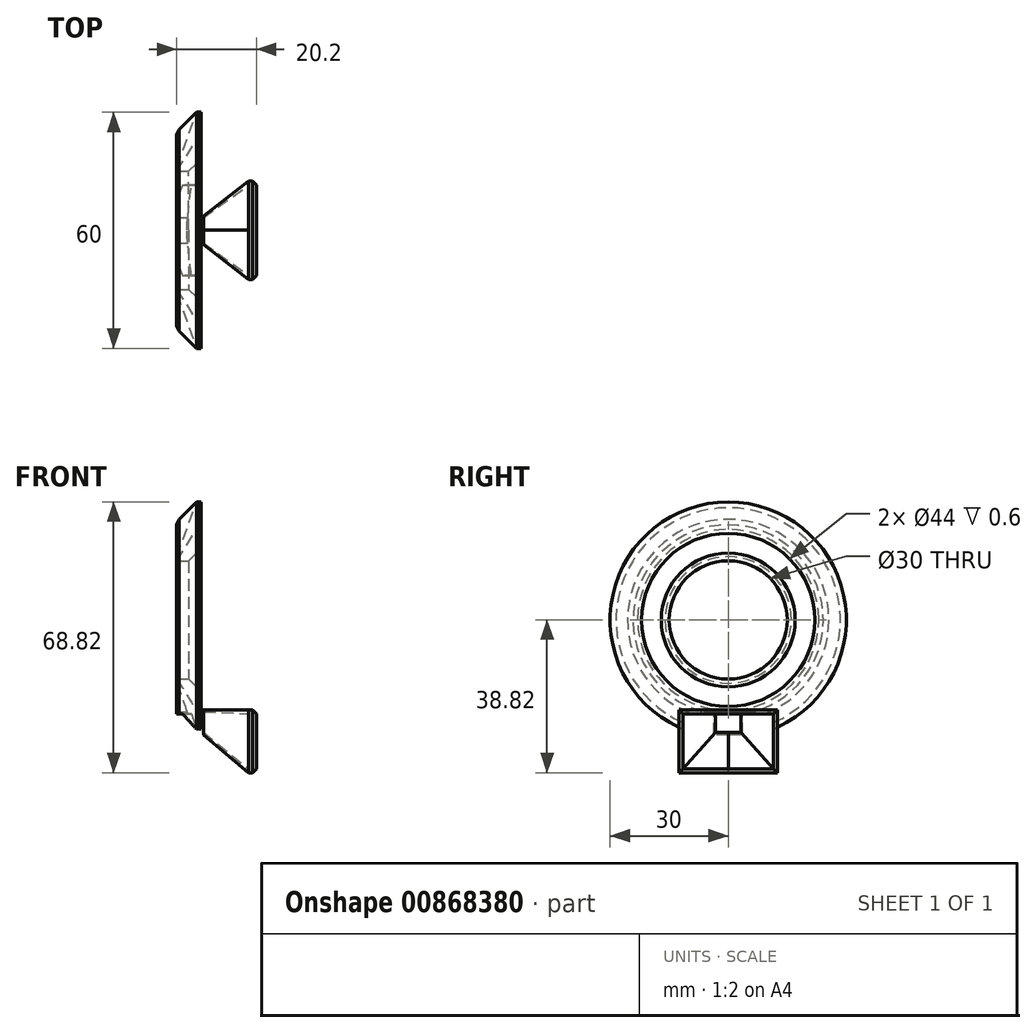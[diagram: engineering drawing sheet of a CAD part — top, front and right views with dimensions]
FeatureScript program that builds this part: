
annotation { "Feature Type Name" : "Feature", "Feature Type Description" : "" }
export const myFeature = defineFeature(function(context is Context, id is Id, definition is map)
    precondition{}
    {
        {
            var Q0;
            Q0=qCreatedBy(makeId("Front.planeOp"),FACE);
            var sketch = newSketch(context, id + "F0", { "sketchPlane" : qUnion([Q0])});
            skLineSegment(sketch, "E0.bottom", {"start": v(-2.5, 15) * mm, "end": v(2.5, 15) * mm});
            skLineSegment(sketch, "E0.top", {"start": v(-2.5, -15) * mm, "end": v(2.5, -15) * mm});
            skLineSegment(sketch, "E0.left", {"start": v(-2.5, 15) * mm, "end": v(-2.5, -15) * mm});
            skLineSegment(sketch, "E0.right", {"start": v(2.5, 15) * mm, "end": v(2.5, -15) * mm});
            skPoint(sketch, "E0.middle", {"position": v(0, 0) * mm});
            skLineSegment(sketch, "E1", {"start": v(2.5, 23) * mm, "end": v(2.5, 15) * mm});
            skLineSegment(sketch, "E2", {"start": v(-8.2, -15) * mm, "end": v(-8.2, 23) * mm});
            skLineSegment(sketch, "E3", {"start": v(2.5, 23) * mm, "end": v(-2.5, 15) * mm});
            skLineSegment(sketch, "E4", {"start": v(-2.5, 15) * mm, "end": v(-2.5, 30) * mm});
            skLineSegment(sketch, "E5", {"start": v(-2.5, 16.07) * mm, "end": v(2.5, 30) * mm});
            skLineSegment(sketch, "E6", {"start": v(-2.5, 30) * mm, "end": v(2.5, 30) * mm});
            skLineSegment(sketch, "E7", {"start": v(2.5, 0) * mm, "end": v(-2.5, 0) * mm});
            skLineSegment(sketch, "E8.bottom", {"start": v(2.5, 15) * mm, "end": v(-2.5, 15) * mm});
            skLineSegment(sketch, "E8.top", {"start": v(2.5, 12.99) * mm, "end": v(-2.5, 12.99) * mm});
            skLineSegment(sketch, "E8.left", {"start": v(2.5, 15) * mm, "end": v(2.5, 12.99) * mm});
            skLineSegment(sketch, "E8.right", {"start": v(-2.5, 15) * mm, "end": v(-2.5, 12.99) * mm});
            skSolve(sketch);
        }
        {
            var Q0;
            {var subQ2=sQuery(id+"F0.wireOp",EDGE,"E5");Q0=makeQuery(id+"F0.imprint","IMPRINT",FACE,{"disambiguationData":[TD([[makeQuery(id+"F0.imprint","IMPRINT",EDGE,{"derivedFrom":subQ2}),1.0]])]});}
            var Q1;
            Q1=makeQuery(id+"F0.imprint","IMPRINT",FACE,{"disambiguationData":[TD([[makeQuery(id+"F0.imprint","IMPRINT",EDGE,{"derivedFrom":sQuery(id+"F0.wireOp",EDGE,"E0.bottom")}),1.0]])]});
            var Q2;
            Q2=makeQuery(id+"F0.imprint","IMPRINT",FACE,{"disambiguationData":[TD([[makeQuery(id+"F0.imprint","IMPRINT",EDGE,{"derivedFrom":sQuery(id+"F0.wireOp",EDGE,"E8.bottom")}),1.0]])]});
            var Q3;
            Q3=makeQuery(id+"F0.imprint","IMPRINT",FACE,{"disambiguationData":[TD([[makeQuery(id+"F0.imprint","IMPRINT",EDGE,{"derivedFrom":sQuery(id+"F0.wireOp",EDGE,"E1")}),-1.0]])]});
            var Q4;
            Q4=sQuery(id+"F0.wireOp",EDGE,"E7");
            revolve(context, id + "F1", {"surfaceOperationType" : NewSurfaceOperationType.NEW, "entities" : qUnion([Q0, Q1, Q2, Q3]), "axis" : qUnion([Q4]), "revolveType" : RevolveType.FULL});
        }
        {
            var Q0;
            Q0=makeQuery(id+"F1.opRevolve","SWEPT_EDGE",EDGE,{"disambiguationData":[OSD([sQuery(id+"F0.wireOp",EDGE,"E4"),sQuery(id+"F0.wireOp",EDGE,"E6")])]});
            chamfer(context, id + "F2", {"entities" : qUnion([Q0]), "width" : 5 * mm, "tangentPropagation" : true});
        }
        {
            var Q0;
            Q0=makeQuery(id+"F1.opRevolve","SWEPT_EDGE",EDGE,{"disambiguationData":[OSD([sQuery(id+"F0.wireOp",EDGE,"E0.right"),sQuery(id+"F0.wireOp",EDGE,"E8.top"),sQuery(id+"F0.wireOp",EDGE,"E8.left")])]});
            chamfer(context, id + "F3", {"entities" : qUnion([Q0]), "width" : 2 * mm, "tangentPropagation" : true});
        }
        {
            var Q0;
            {var subQ0=sQuery(id+"F0.wireOp",EDGE,"E4");Q0=makeQuery(id+"F2.opChamfer","BLEND_EDGE",EDGE,{"blendedFrom":[makeQuery(id+"F1.opRevolve","SWEPT_EDGE",EDGE,{"disambiguationData":[OSD([subQ0,sQuery(id+"F0.wireOp",EDGE,"E6")])]}),makeQuery(id+"F1.opRevolve","SWEPT_FACE",FACE,{"disambiguationData":[OSD([subQ0])]})],"blendedInto":[makeQuery(id+"F1.opRevolve","SWEPT_FACE",FACE,{"disambiguationData":[OSD([subQ0])]})]});}
            chamfer(context, id + "F4", {"entities" : qUnion([Q0]), "width" : 2 * mm, "tangentPropagation" : true});
        }
        {
            var Q0;
            Q0=makeQuery(id+"F1.opRevolve","SWEPT_FACE",FACE,{"disambiguationData":[OSD([sQuery(id+"F0.wireOp",EDGE,"E1"),sQuery(id+"F0.wireOp",EDGE,"E8.left")])]});
            var sketch = newSketch(context, id + "F5", { "sketchPlane" : qUnion([Q0])});
            skCircle(sketch, "E9", {"center": v(0, 0) * mm, "radius": 23 * mm});
            skCircle(sketch, "E10", {"center": v(0, 0) * mm, "radius": 22 * mm});
            skCircle(sketch, "E11", {"center": v(0, 0) * mm, "radius": 30 * mm});
            skCircle(sketch, "E12", {"center": v(0, 0) * mm, "radius": 28.5 * mm});
            skSolve(sketch);
        }
        {
            var Q0;
            Q0=makeQuery(id+"F5.imprint","IMPRINT",FACE,{"disambiguationData":[TD([[makeQuery(id+"F5.imprint","IMPRINT",EDGE,{"derivedFrom":sQuery(id+"F5.wireOp",EDGE,"E9")}),1.0]])]});
            var Q1;
            Q1=makeQuery(id+"F5.imprint","IMPRINT",FACE,{"disambiguationData":[TD([[makeQuery(id+"F5.imprint","IMPRINT",EDGE,{"derivedFrom":sQuery(id+"F5.wireOp",EDGE,"E11")}),1.0]])]});
            extrude(context, id + "F6", {"entities" : qUnion([Q0, Q1]), "operationType" : NewBodyOperationType.ADD, "depth" : .6 * mm, "offsetDistance" : 25 * mm});
        }
        {
            var Q0;
            Q0=makeQuery(id+"F6.opExtrude","CAP_FACE",FACE,{"disambiguationData":[OSD([sQuery(id+"F5.wireOp",EDGE,"E9"),sQuery(id+"F5.wireOp",EDGE,"E10")])],"isStart":false});
            var sketch = newSketch(context, id + "F7", { "sketchPlane" : qUnion([Q0])});
            skCircle(sketch, "E13", {"center": v(0, 0) * mm, "radius": 30 * mm});
            skCircle(sketch, "E14", {"center": v(0, 0) * mm, "radius": 22 * mm});
            skSolve(sketch);
        }
        {
            var Q0;
            Q0 = qSketchRegion(id + "F7", true);
            extrude(context, id + "F8", {"entities" : qUnion([Q0]), "depth" : .6 * mm, "offsetDistance" : 25 * mm});
        }
        {
            var Q0;
            Q0=makeQuery(id+"F8.opExtrude","CAP_FACE",FACE,{"disambiguationData":[OSD([sQuery(id+"F7.wireOp",EDGE,"E13"),sQuery(id+"F7.wireOp",EDGE,"E14")])],"isStart":false});
            var sketch = newSketch(context, id + "F9", { "sketchPlane" : qUnion([Q0])});
            skLineSegment(sketch, "E15", {"start": v(0, -30) * mm, "end": v(0, -22) * mm});
            skLineSegment(sketch, "E16.bottom", {"start": v(3.6, -29.18) * mm, "end": v(-3.6, -29.18) * mm});
            skLineSegment(sketch, "E16.top", {"start": v(3.6, -22.82) * mm, "end": v(-3.6, -22.82) * mm});
            skLineSegment(sketch, "E16.left", {"start": v(3.6, -29.18) * mm, "end": v(3.6, -22.82) * mm});
            skLineSegment(sketch, "E16.right", {"start": v(-3.6, -29.18) * mm, "end": v(-3.6, -22.82) * mm});
            skPoint(sketch, "E16.middle", {"position": v(0, -26) * mm});
            skSolve(sketch);
        }
        {
            var Q0;
            Q0 = qSketchRegion(id + "F9", true);
            extrude(context, id + "F10", {"entities" : qUnion([Q0]), "operationType" : NewBodyOperationType.ADD, "depth" : .6 * mm, "offsetDistance" : 25 * mm});
        }
        {
            var Q0;
            Q0=makeQuery(id+"F10.opExtrude","SWEPT_FACE",FACE,{"disambiguationData":[OSD([sQuery(id+"F9.wireOp",EDGE,"E16.top")])]});
            var sketch = newSketch(context, id + "F11", { "sketchPlane" : qUnion([Q0])});
            skLineSegment(sketch, "E17.bottom", {"start": v(17.44, -6.08) * mm, "end": v(-9.45, -6.08) * mm});
            skLineSegment(sketch, "E17.top", {"start": v(17.44, 12.53) * mm, "end": v(-9.45, 12.53) * mm});
            skLineSegment(sketch, "E17.left", {"start": v(17.44, -6.08) * mm, "end": v(17.44, 12.53) * mm});
            skLineSegment(sketch, "E17.right", {"start": v(-9.45, -6.08) * mm, "end": v(-9.45, 12.53) * mm});
            skPoint(sketch, "E17.middle", {"position": v(4, 3.23) * mm});
            skLineSegment(sketch, "E18", {"start": v(3.7, 0) * mm, "end": v(16.7, 0) * mm});
            skLineSegment(sketch, "E19.bottom", {"start": v(15.7, 12.5) * mm, "end": v(17.7, 12.5) * mm});
            skLineSegment(sketch, "E19.top", {"start": v(15.7, -12.5) * mm, "end": v(17.7, -12.5) * mm});
            skLineSegment(sketch, "E19.left", {"start": v(15.7, 12.5) * mm, "end": v(15.7, -12.5) * mm});
            skLineSegment(sketch, "E19.right", {"start": v(17.7, 12.5) * mm, "end": v(17.7, -12.5) * mm});
            skPoint(sketch, "E19.middle", {"position": v(16.7, 0) * mm});
            skSolve(sketch);
        }
        {
            var Q0;
            {var subQ3=sQuery(id+"F11.wireOp",EDGE,"E19.bottom");Q0=makeQuery(id+"F11.imprint","IMPRINT",FACE,{"disambiguationData":[TD([[makeQuery(id+"F11.imprint","IMPRINT",EDGE,{"derivedFrom":subQ3}),-1.0]])]});}
            var Q1;
            {var subQ5=sQuery(id+"F11.wireOp",EDGE,"E19.top");Q1=makeQuery(id+"F11.imprint","IMPRINT",FACE,{"disambiguationData":[TD([[makeQuery(id+"F11.imprint","IMPRINT",EDGE,{"derivedFrom":subQ5}),1.0]])]});}
            extrude(context, id + "F12", {"entities" : qUnion([Q0, Q1]), "operationType" : NewBodyOperationType.ADD, "depth" : -16 * mm, "offsetDistance" : 25 * mm});
        }
        {
            var Q0;
            Q0=makeQuery(id+"F10.opExtrude","CAP_FACE",FACE,{"disambiguationData":[OSD([sQuery(id+"F9.wireOp",EDGE,"E16.bottom"),sQuery(id+"F9.wireOp",EDGE,"E16.top"),sQuery(id+"F9.wireOp",EDGE,"E16.left"),sQuery(id+"F9.wireOp",EDGE,"E16.right")])],"isStart":false});
            var sketch = newSketch(context, id + "F13", { "sketchPlane" : qUnion([Q0])});
            skLineSegment(sketch, "E20", {"start": v(0, -22.82) * mm, "end": v(0, -29.18) * mm});
            skLineSegment(sketch, "E21.bottom", {"start": v(-3.23, -28.62) * mm, "end": v(3.23, -28.62) * mm});
            skLineSegment(sketch, "E21.top", {"start": v(-3.23, -23.38) * mm, "end": v(3.23, -23.38) * mm});
            skLineSegment(sketch, "E21.left", {"start": v(-3.23, -28.62) * mm, "end": v(-3.23, -23.38) * mm});
            skLineSegment(sketch, "E21.right", {"start": v(3.23, -28.62) * mm, "end": v(3.23, -23.38) * mm});
            skPoint(sketch, "E21.middle", {"position": v(0, -26) * mm});
            skSolve(sketch);
        }
        {
            var Q0;
            Q0=makeQuery(id+"F12.opExtrude","SWEPT_FACE",FACE,{"disambiguationData":[OSD([sQuery(id+"F11.wireOp",EDGE,"E19.left")])]});
            var sketch = newSketch(context, id + "F14", { "sketchPlane" : qUnion([Q0])});
            skLineSegment(sketch, "E22", {"start": v(0, -38.82) * mm, "end": v(0, -22.82) * mm});
            skLineSegment(sketch, "E23.bottom", {"start": v(11.5, -37.82) * mm, "end": v(-11.5, -37.82) * mm});
            skLineSegment(sketch, "E23.top", {"start": v(11.5, -23.82) * mm, "end": v(-11.5, -23.82) * mm});
            skLineSegment(sketch, "E23.left", {"start": v(11.5, -37.82) * mm, "end": v(11.5, -23.82) * mm});
            skLineSegment(sketch, "E23.right", {"start": v(-11.5, -37.82) * mm, "end": v(-11.5, -23.82) * mm});
            skPoint(sketch, "E23.middle", {"position": v(0, -30.82) * mm});
            skSolve(sketch);
        }
        {
            var Q0;
            Q0=makeQuery(id+"F12.opExtrude","SWEPT_FACE",FACE,{"disambiguationData":[OSD([sQuery(id+"F11.wireOp",EDGE,"E19.right")])]});
            var sketch = newSketch(context, id + "F15", { "sketchPlane" : qUnion([Q0])});
            skLineSegment(sketch, "E24", {"start": v(0, -22.82) * mm, "end": v(0, -38.82) * mm});
            skLineSegment(sketch, "E25.bottom", {"start": v(-11.5, -23.82) * mm, "end": v(11.5, -23.82) * mm});
            skLineSegment(sketch, "E25.top", {"start": v(-11.5, -37.82) * mm, "end": v(11.5, -37.82) * mm});
            skLineSegment(sketch, "E25.left", {"start": v(-11.5, -23.82) * mm, "end": v(-11.5, -37.82) * mm});
            skLineSegment(sketch, "E25.right", {"start": v(11.5, -23.82) * mm, "end": v(11.5, -37.82) * mm});
            skPoint(sketch, "E25.middle", {"position": v(0, -30.82) * mm});
            skSolve(sketch);
        }
        {
            var Q0;
            {var subQ5=sQuery(id+"F15.wireOp",EDGE,"E25.right");Q0=makeQuery(id+"F15.imprint","IMPRINT",FACE,{"disambiguationData":[TD([[makeQuery(id+"F15.imprint","IMPRINT",EDGE,{"derivedFrom":subQ5}),-1.0]])]});}
            var Q1;
            {var subQ5=sQuery(id+"F15.wireOp",EDGE,"E25.left");Q1=makeQuery(id+"F15.imprint","IMPRINT",FACE,{"disambiguationData":[TD([[makeQuery(id+"F15.imprint","IMPRINT",EDGE,{"derivedFrom":subQ5}),1.0]])]});}
            extrude(context, id + "F16", {"entities" : qUnion([Q0, Q1]), "operationType" : NewBodyOperationType.REMOVE, "oppositeDirection" : true, "depth" : 25 * mm, "offsetDistance" : 25 * mm});
        }
        {
            var Q2;
            {var subQ5=sQuery(id+"F14.wireOp",EDGE,"E23.left");Q2=makeQuery(id+"F14.imprint","IMPRINT",FACE,{"disambiguationData":[TD([[makeQuery(id+"F14.imprint","IMPRINT",EDGE,{"derivedFrom":subQ5}),1.0]])]});}
            var Q3;
            {var subQ5=sQuery(id+"F13.wireOp",EDGE,"E21.left");Q3=makeQuery(id+"F13.imprint","IMPRINT",FACE,{"disambiguationData":[TD([[makeQuery(id+"F13.imprint","IMPRINT",EDGE,{"derivedFrom":subQ5}),-1.0]])]});}
            loft(context, id + "F17", {"operationType" : NewBodyOperationType.REMOVE, "sheetProfilesArray" : [{ "sheetProfileEntities" : qUnion([Q2]) }, { "sheetProfileEntities" : qUnion([Q3]) }]});
        }
        {
            var Q0;
            {var subQ5=sQuery(id+"F13.wireOp",EDGE,"E21.left");Q0=makeQuery(id+"F13.imprint","IMPRINT",FACE,{"disambiguationData":[TD([[makeQuery(id+"F13.imprint","IMPRINT",EDGE,{"derivedFrom":subQ5}),-1.0]])]});}
            var Q1;
            {var subQ5=sQuery(id+"F13.wireOp",EDGE,"E21.right");Q1=makeQuery(id+"F13.imprint","IMPRINT",FACE,{"disambiguationData":[TD([[makeQuery(id+"F13.imprint","IMPRINT",EDGE,{"derivedFrom":subQ5}),1.0]])]});}
            extrude(context, id + "F18", {"entities" : qUnion([Q0, Q1]), "operationType" : NewBodyOperationType.REMOVE, "oppositeDirection" : true, "depth" : 25 * mm, "offsetDistance" : 25 * mm});
        }
        {
            var Q0;
            {var subQ0=sQuery(id+"F13.wireOp",EDGE,"E21.left");Q0=makeQuery(id+"F13.imprint","IMPRINT",FACE,{"disambiguationData":[TD([[makeQuery(id+"F13.imprint","IMPRINT",EDGE,{"derivedFrom":subQ0}),1.0]])]});}
            var Q1;
            {var subQ0=sQuery(id+"F14.wireOp",EDGE,"E23.left");Q1=makeQuery(id+"F14.imprint","IMPRINT",FACE,{"disambiguationData":[TD([[makeQuery(id+"F14.imprint","IMPRINT",EDGE,{"derivedFrom":subQ0}),-1.0]])]});}
            loft(context, id + "F19", {"sheetProfilesArray" : [{ "sheetProfileEntities" : qUnion([Q0]) }, { "sheetProfileEntities" : qUnion([Q1]) }]});
        }
        {
            var Q0;
            {var subQ0=sQuery(id+"F13.wireOp",EDGE,"E21.right");Q0=makeQuery(id+"F13.imprint","IMPRINT",FACE,{"disambiguationData":[TD([[makeQuery(id+"F13.imprint","IMPRINT",EDGE,{"derivedFrom":subQ0}),-1.0]])]});}
            var Q1;
            {var subQ0=sQuery(id+"F14.wireOp",EDGE,"E23.right");Q1=makeQuery(id+"F14.imprint","IMPRINT",FACE,{"disambiguationData":[TD([[makeQuery(id+"F14.imprint","IMPRINT",EDGE,{"derivedFrom":subQ0}),1.0]])]});}
            loft(context, id + "F20", {"sheetProfilesArray" : [{ "sheetProfileEntities" : qUnion([Q0]) }, { "sheetProfileEntities" : qUnion([Q1]) }]});
        }
        {
            var Q0;
            Q0=makeQuery(id+"F12.opExtrude","CAP_EDGE",EDGE,{"disambiguationData":[OSD([sQuery(id+"F11.wireOp",EDGE,"E19.right")])],"isStart":true});
            var Q1;
            Q1=makeQuery(id+"F12.opExtrude","CAP_EDGE",EDGE,{"disambiguationData":[OSD([sQuery(id+"F11.wireOp",EDGE,"E19.right")])],"isStart":false});
            var Q2;
            Q2=makeQuery(id+"F12.opExtrude","SWEPT_EDGE",EDGE,{"disambiguationData":[OSD([sQuery(id+"F11.wireOp",EDGE,"E19.top"),sQuery(id+"F11.wireOp",EDGE,"E19.right")])]});
            var Q3;
            Q3=makeQuery(id+"F12.opExtrude","SWEPT_EDGE",EDGE,{"disambiguationData":[OSD([sQuery(id+"F11.wireOp",EDGE,"E19.bottom"),sQuery(id+"F11.wireOp",EDGE,"E19.right")])]});
            chamfer(context, id + "F21", {"entities" : qUnion([Q0, Q1, Q2, Q3]), "width" : 1 * mm, "tangentPropagation" : true});
        }
    });
